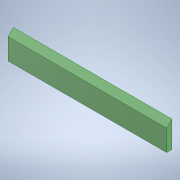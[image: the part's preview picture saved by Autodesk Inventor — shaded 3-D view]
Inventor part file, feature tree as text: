
AUTODESK INVENTOR PART (.ipt)
format: ipt  version: 2020 (Build 240168000, 168)  size: 100,864 bytes
history: native  units: mm
features: extrude x1, chamfer x1, thicken_offset x1, sketch x1
ambient origin geometry x8: Origin, YZ Plane, XZ Plane, XY Plane, X Axis, Y Axis, Z Axis, Center Point
bodies: Solid1 (feature_tree)
feature tree (4):
  extrude  "Extrusion1"  Depth=10.0mm
  chamfer  "Chamfer1"  Distance=10.0mm
  thicken_offset  "Thicken1"
  sketch  "Sketch1"  dims[d0=300.0mm d1=30.0mm d2=10.0mm d3=0.0mm d4=10.0mm d5=2.0mm d6=45.0deg d7=20.0mm d8=20.0mm]
